# Revit family: Toilet-Elongated-American_Standard-Afwall_Retrofit-2294011EC.020
name_source: partatom
category: Plumbing Fixtures
revit_build: Autodesk Revit 2018 (Build: 20170223_1515(x64)
units: mm (PartAtom-declared; Revit-internal decimal feet)

## family parameters
Cut with Voids When Loaded = No
Host = Face
OmniClass Number = 23.45.05.21.11.11
OmniClass Title = Water Operated Water Closets
Part Type = Normal
Room Calculation Point = No
Round Connector Dimension = Use Radius
Shared = Yes

## types (2) — shared parameters
047007-0070A Inlet spud = Yes
736046-100 Flushometer valve rough-in adapter kit = Yes
ADA Compliant = Yes
Assembly Code = D2010110
Bowl Shape = Elongated
CEC Compliant = Yes
CW Connection = Yes
CWFU = 5
Carrier Fitting J.R. Smith 210L or equal = No
Cold Water Connection Diameter = 1"
Cold Water Connection Height = 26 1/2"
Cold Water Connection Radius = 1/2"
Compliance Certifications = ASME A112.19.2-2008/CSA B45.1-08 for Vitreous China Fixtures
Default Elevation = 16 1/8"
Description = Afwall® ADA Retrofit 1.28 – 1.6 gpf (4.8 – 6.0 Lpf) Top Spud Elongated Wall-Hung EverClean® Bowl
Finish = Vitreous China-American Standard-020-White
Flush Rate = 1.28 gpf (4.8 Lpf) to 1.6 gpf (6.0 Lpf)
Flushometer Valve- 1.28 gpf- Manual- American Standard 6047.121.002 (Top Spud) = No
Flushometer Valve- 1.28 gpf- Sensor-Operated- American Standard Selectronic®DC Power 6065.121.002 (Top Spud) = No
Flushometer Valve- 1.6 gpf- Manual- American Standard 6047.161.002 (Top Spud) = No
Flushometer Valve- 1.6 gpf- Sensor-Operated- American Standard Selectronic®DC Power 6065.161.002 (Top Spud) = No
HW Connection = No
Height = 14 1/2"
Installation Type = Wall Mounted
Length = 25"
Manufacturer = American Standard
Material = Vitreous China-American Standard-020-White
Model = 2294011EC.020
Price = Prices may vary. Please consult Manufacturer Representative for most up-to-date price list.
Product Documentation Link = https://americanstandard.box.com
Product Page URL = https://www.americanstandard-us.com
Revised Date = 08/10/2022
Seat - American Standard 5901.100 Heavy duty open front less cover = No
Seat - American Standard 5905.100 Extra heavy duty open front less cover = No
Seat - American Standard 5905.110 Extra heavy duty open front less cover with EverClean®Surface = No
URL = http://www.americanstandard-us.com
Vent Connection = No
WFU = 5
Waste Connection = Yes
Waste Connection Diameter = 2 1/8"
Waste Connection Height = 5 1/4"
Waste Connection Radius = 1 1/16"
Width = 14 3/4"
zero-valued in all types: HWFU

## per-type parameters (varying)
| type | Slotted Rim | Type Comments |
| 2294011EC.020 | No | Elongated bowl only, top spud |
| 2296.019EC.020 | Yes | Elongated bowl only, top spud with slotted rim for bedpan holding |

## geometry (parser evidence)
native form markers: Sweep x5
no freeform markers — native parametric forms only
